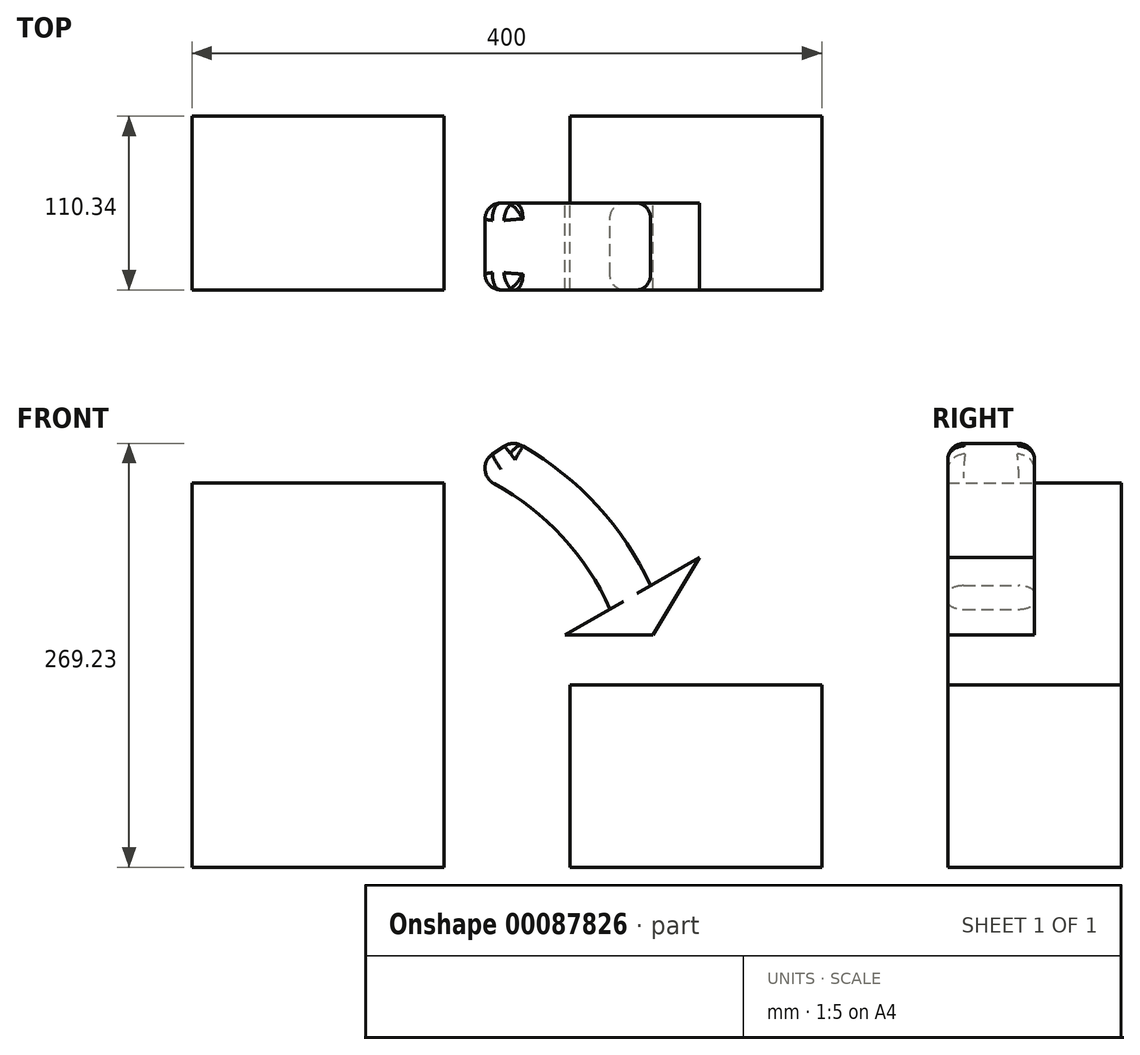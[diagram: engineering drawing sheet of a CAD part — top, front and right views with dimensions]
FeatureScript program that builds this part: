
annotation { "Feature Type Name" : "Feature", "Feature Type Description" : "" }
export const myFeature = defineFeature(function(context is Context, id is Id, definition is map)
    precondition{}
    {
        {
            var Q0;
            Q0=qCreatedBy(makeId("Front.planeOp"),FACE);
            var sketch = newSketch(context, id + "F0", { "sketchPlane" : qUnion([Q0])});
            skLineSegment(sketch, "E0.bottom", {"start": v(-200, 0) * mm, "end": v(-40, 0) * mm});
            skLineSegment(sketch, "E0.top", {"start": v(-200, 244) * mm, "end": v(-40, 244) * mm});
            skLineSegment(sketch, "E0.left", {"start": v(-200, 0) * mm, "end": v(-200, 244) * mm});
            skLineSegment(sketch, "E0.right", {"start": v(-40, 0) * mm, "end": v(-40, 244) * mm});
            skLineSegment(sketch, "E1.bottom", {"start": v(40, 0) * mm, "end": v(200, 0) * mm});
            skLineSegment(sketch, "E1.top", {"start": v(40, 115.9) * mm, "end": v(200, 115.9) * mm});
            skLineSegment(sketch, "E1.left", {"start": v(40, 0) * mm, "end": v(40, 115.9) * mm});
            skLineSegment(sketch, "E1.right", {"start": v(200, 0) * mm, "end": v(200, 115.9) * mm});
            skSolve(sketch);
        }
        {
            var Q0;
            Q0=makeQuery(id+"F0.imprint","IMPRINT",FACE,{"disambiguationData":[TD([[makeQuery(id+"F0.imprint","IMPRINT",EDGE,{"derivedFrom":sQuery(id+"F0.wireOp",EDGE,"E0.bottom")}),1.0]])]});
            var Q1;
            Q1=makeQuery(id+"F0.imprint","IMPRINT",FACE,{"disambiguationData":[TD([[makeQuery(id+"F0.imprint","IMPRINT",EDGE,{"derivedFrom":sQuery(id+"F0.wireOp",EDGE,"E1.bottom")}),1.0]])]});
            extrude(context, id + "F1", {"entities" : qUnion([Q0, Q1]), "endBound" : BoundingType.SYMMETRIC, "depth" : 110.34 * mm});
        }
        {
            var Q0;
            Q0=qCreatedBy(makeId("Front.planeOp"),FACE);
            var sketch = newSketch(context, id + "F2", { "sketchPlane" : qUnion([Q0])});
            skLineSegment(sketch, "E2", {"start": v(37.02, 147.43) * mm, "end": v(92.83, 147.43) * mm});
            skLineSegment(sketch, "E3", {"start": v(92.83, 147.43) * mm, "end": v(122.25, 196.78) * mm});
            skLineSegment(sketch, "E4", {"start": v(80.51, 174.78) * mm, "end": v(92.83, 147.43) * mm, "construction": true});
            skLineSegment(sketch, "E5", {"start": v(59.22, 159.38) * mm, "end": v(65.48, 163.9) * mm, "construction": true});
            skLineSegment(sketch, "E6", {"start": v(37.02, 147.43) * mm, "end": v(122.25, 196.78) * mm});
            skLineSegment(sketch, "E7", {"start": v(3.67, 271.1) * mm, "end": v(-25.1, 251.72) * mm});
            skArc(sketch, "E8", {"start": v(65.48, 163.9) * mm, "mid": v(28.72, 216.61) * mm, "end": v(-25.1, 251.72) * mm});
            skArc(sketch, "E9.0", {"start": v(91.34, 178.89) * mm, "mid": v(55.1, 232.22) * mm, "end": v(3.67, 271.1) * mm});
            skSolve(sketch);
        }
        {
            var Q0;
            {var subQ0=sQuery(id+"F2.wireOp",EDGE,"KrbDRa1t-sssX-kxbc-dxMV-6ORp5Z4Jm5SW");Q0=makeQuery(id+"F2.imprint","IMPRINT",FACE,{"disambiguationData":[TD([[makeQuery(id+"F2.imprint","IMPRINT",EDGE,{"derivedFrom":subQ0}),1.0]])]});}
            var Q1;
            {var subQ3=sQuery(id+"F2.wireOp",EDGE,"E2");Q1=makeQuery(id+"F2.imprint","IMPRINT",FACE,{"disambiguationData":[TD([[makeQuery(id+"F2.imprint","IMPRINT",EDGE,{"derivedFrom":subQ3}),1.0]])]});}
            var Q2;
            Q2=makeQuery(id+"F2.imprint","IMPRINT",FACE,{"disambiguationData":[TD([[makeQuery(id+"F2.imprint","IMPRINT",EDGE,{"derivedFrom":sQuery(id+"F2.wireOp",EDGE,"E7")}),1.0]])]});
            var Q3;
            Q3=makeQuery(id+"F1.opExtrude","CAP_FACE",FACE,{"disambiguationData":[OSD([sQuery(id+"F0.wireOp",EDGE,"E0.bottom"),sQuery(id+"F0.wireOp",EDGE,"E0.top"),sQuery(id+"F0.wireOp",EDGE,"E0.left"),sQuery(id+"F0.wireOp",EDGE,"E0.right")])],"isStart":false});
            extrude(context, id + "F3", {"entities" : qUnion([Q0, Q1, Q2]), "endBound" : BoundingType.UP_TO_SURFACE, "endBoundEntityFace" : qUnion([Q3]), "depth" : 25 * mm});
        }
        {
            var Q0;
            Q0=makeQuery(id+"F3.opExtrude","SWEPT_EDGE",EDGE,{"disambiguationData":[OSD([sQuery(id+"F2.wireOp",EDGE,"E7"),sQuery(id+"F2.wireOp",EDGE,"E9.0")])]});
            var Q1;
            Q1=makeQuery(id+"F3.opExtrude","CAP_EDGE",EDGE,{"disambiguationData":[OSD([sQuery(id+"F2.wireOp",EDGE,"E7")])],"isStart":false});
            var Q2;
            Q2=makeQuery(id+"F3.opExtrude","SWEPT_EDGE",EDGE,{"disambiguationData":[OSD([sQuery(id+"F2.wireOp",EDGE,"E7"),sQuery(id+"F2.wireOp",EDGE,"E8")])]});
            var Q3;
            Q3=makeQuery(id+"F3.opExtrude","CAP_EDGE",EDGE,{"disambiguationData":[OSD([sQuery(id+"F2.wireOp",EDGE,"E7")])],"isStart":true});
            fillet(context, id + "F4", {"entities" : qUnion([Q0, Q1, Q2, Q3]), "radius" : 11.02 * mm, "tangentPropagation" : true, "allowEdgeOverflow" : false});
        }
        {
            var Q0;
            Q0=makeQuery(id+"F3.opExtrude","CAP_EDGE",EDGE,{"disambiguationData":[OSD([sQuery(id+"F2.wireOp",EDGE,"E9.0")])],"isStart":false});
            var Q1;
            Q1=makeQuery(id+"F3.opExtrude","CAP_EDGE",EDGE,{"disambiguationData":[OSD([sQuery(id+"F2.wireOp",EDGE,"E8")])],"isStart":false});
            var Q2;
            Q2=makeQuery(id+"F3.opExtrude","CAP_EDGE",EDGE,{"disambiguationData":[OSD([sQuery(id+"F2.wireOp",EDGE,"E8")])],"isStart":true});
            var Q3;
            Q3=makeQuery(id+"F3.opExtrude","CAP_EDGE",EDGE,{"disambiguationData":[OSD([sQuery(id+"F2.wireOp",EDGE,"E9.0")])],"isStart":true});
            fillet(context, id + "F5", {"entities" : qUnion([Q0, Q1, Q2, Q3]), "radius" : 10 * mm, "tangentPropagation" : true, "allowEdgeOverflow" : false});
        }
    });
